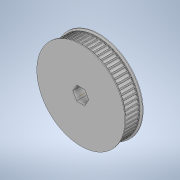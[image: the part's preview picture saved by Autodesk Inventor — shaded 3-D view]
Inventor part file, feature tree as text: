
AUTODESK INVENTOR PART (.ipt)
format: ipt  version: 2022.3 (Build 263350000, 350)  size: 518,656 bytes
history: native  units: in
note: dims shown in document units (in); Inventor stores cm internally (conversion verified against a paired STEP export)
features: sketch x7, extrude x6, mirror x2, chamfer x2, other x1, fillet x1, pattern_circular x1
ambient origin geometry x8: Origin, YZ Plane, XZ Plane, XY Plane, X Axis, Y Axis, Z Axis, Center Point
bodies: Solid1 (feature_tree)
feature tree (20):
  other  "Hex Bore"
  extrude  "HTD Base"  Depth=0.3937in TaperAngle=0.0deg
  extrude  "HTD Flange"  Depth=0.0591in
  mirror  "HTD Flanges"
  chamfer  "HTD Flange Chamfer"  Distance=0.0787in Angle=45.0deg
  extrude  "GT2 Base"  TaperAngle=0.0deg  [1 undecoded]
  extrude  "GT2 Base Tooth"  TaperAngle=0.0deg  [1 undecoded]
  fillet  "GT2 Base Tooth pt. 2"  Radius=2.3761in
  pattern_circular  "GT2 Teeth"  [2 undecoded]
  extrude  "GT2 Flange"  Depth=0.0591in
  mirror  "GT2 Flanges"
  chamfer  "GT2 Flange Chamfer"  Distance=0.0075in
  extrude  "Circle Bore"  TaperAngle=0.0deg  [1 undecoded]
  sketch  "Sketch1"  dims[d0=3.9652in d1=0.3937in d2=0.0in]
  sketch  "Sketch3"  dims[d12=0.0394in d13=0.0591in]
  sketch  "Sketch4"  dims[d14=0.0in]
  sketch  "Sketch5"  dims[d15=0.0394in d16=0.0787in d17=45.0deg]
  sketch  "Sketch6"  dims[d18=0.385in d19=0.0in d20=0.0in]
  sketch  "Sketch7"  dims[d21=0.385in d22=0.0in d23=0.0in d24=2.3761in]
  sketch  "Sketch8"  dims[d25=0.3937in d26=0.0in d27=0.0727in d28=0.0075in d29=0.0in d30=0.0in d31=0.0118in d32=25.1969in d33=360.0deg d35=0.0394in d36=0.0591in d37=0.0in d38=0.0394in d39=0.0787in d40=45.0deg]
note: 5 required parameter values undecoded (feature->parameter linkage not recoverable at this tier; creation-order binding heuristic only, values carry confidence <= 0.55)
